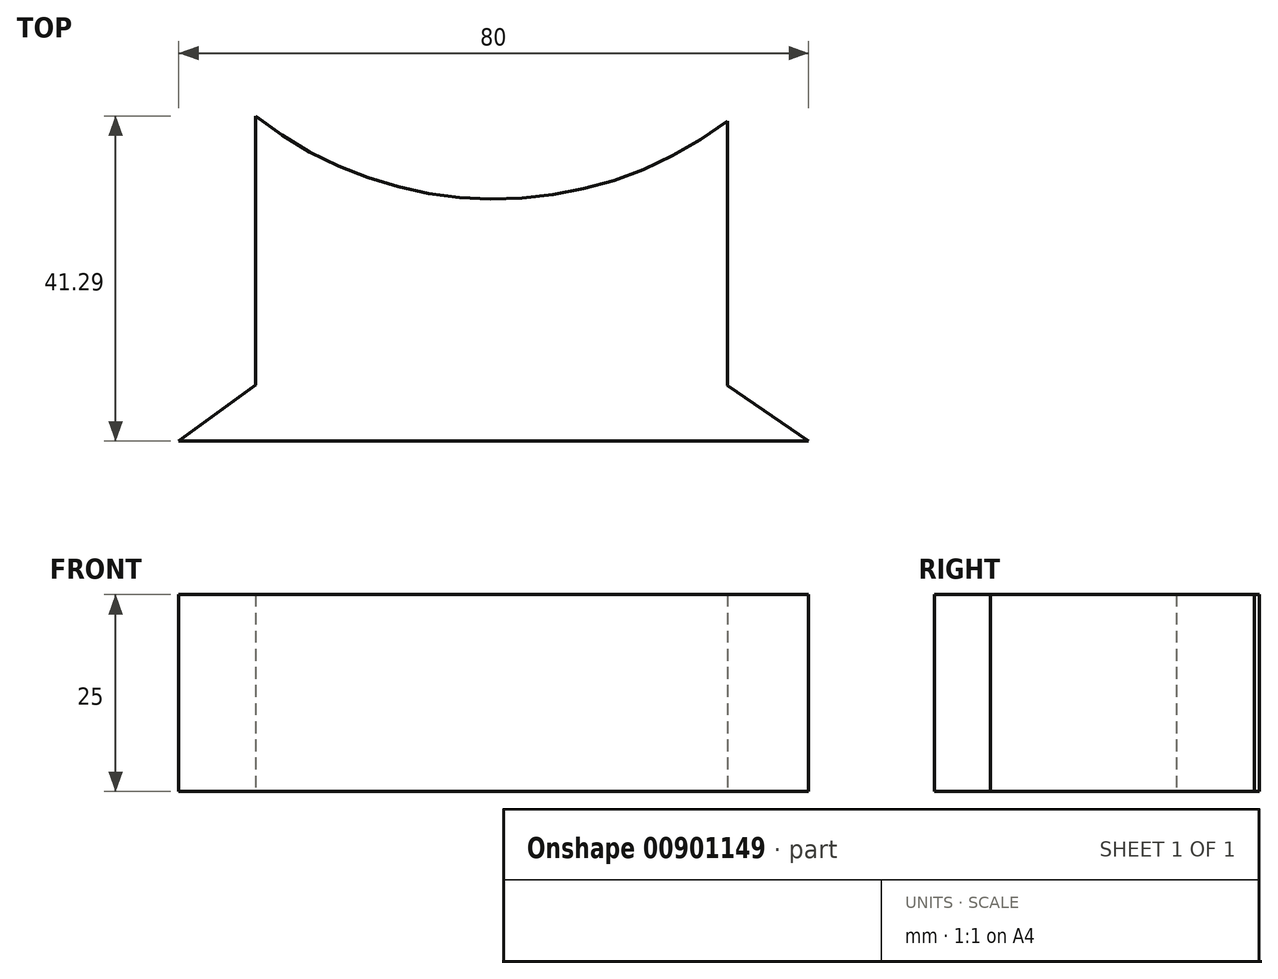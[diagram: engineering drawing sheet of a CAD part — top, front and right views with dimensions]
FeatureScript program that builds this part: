
annotation { "Feature Type Name" : "Feature", "Feature Type Description" : "" }
export const myFeature = defineFeature(function(context is Context, id is Id, definition is map)
    precondition{}
    {
        {
            var Q0;
            Q0=qCreatedBy(makeId("Top.planeOp"),FACE);
            var sketch = newSketch(context, id + "F0", { "sketchPlane" : qUnion([Q0])});
            skLineSegment(sketch, "E0", {"start": v(-63.01, 26.94) * mm, "end": v(16.99, 26.94) * mm});
            skLineSegment(sketch, "E1", {"start": v(-63.01, 26.94) * mm, "end": v(-53.22, 34.05) * mm});
            skLineSegment(sketch, "E2", {"start": v(-53.22, 34.05) * mm, "end": v(-53.22, 68.23) * mm});
            skLineSegment(sketch, "E3", {"start": v(-53.22, 34.05) * mm, "end": v(-52.8, 34.05) * mm});
            skLineSegment(sketch, "E4", {"start": v(16.99, 26.94) * mm, "end": v(6.68, 34.03) * mm});
            skLineSegment(sketch, "E5", {"start": v(6.68, 34.03) * mm, "end": v(6.68, 67.58) * mm});
            skArc(sketch, "E6", {"start": v(-53.22, 68.23) * mm, "mid": v(-23.39, 57.68) * mm, "end": v(6.68, 67.58) * mm});
            skSolve(sketch);
        }
        {
            var Q0;
            Q0=makeQuery(id+"F0.imprint","IMPRINT",FACE,{"disambiguationData":[TD([[makeQuery(id+"F0.imprint","IMPRINT",EDGE,{"derivedFrom":sQuery(id+"F0.wireOp",EDGE,"E0")}),1.0]])]});
            extrude(context, id + "F1", {"entities" : qUnion([Q0]), "depth" : 25 * mm, "offsetDistance" : 25 * mm});
        }
    });
